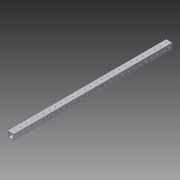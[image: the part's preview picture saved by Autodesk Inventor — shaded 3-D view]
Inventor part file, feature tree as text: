
AUTODESK INVENTOR PART (.ipt)
format: ipt  version: 2014 SP1 (Build 180222100, 222)  size: 189,440 bytes
history: native  units: in
note: dims shown in document units (in); Inventor stores cm internally (conversion verified against a paired STEP export)
features: extrude x3, sketch x3, pattern_linear x2
ambient origin geometry x8: Origin, YZ Plane, XZ Plane, XY Plane, X Axis, Y Axis, Z Axis, Center Point
bodies: Solid1 (feature_tree)
feature tree (8):
  extrude  "Extrusion1"  Depth=1.0in
  extrude  "Extrusion2"  Depth=27.125in TaperAngle=0.0deg
  sketch  "Sketch2"  dims[d2=0.125in d3=27.125in d4=0.0in]
  pattern_linear  "Rectangular Pattern1"  Spacing1=0.164in  [1 undecoded]
  extrude  "Extrusion3"  Depth=1.0in TaperAngle=0.0deg
  pattern_linear  "Rectangular Pattern2"  Count1=27 Spacing1=1.0in
  sketch  "Sketch1"  dims[d0=1.0in d1=1.0in]
  sketch  "Sketch3"  dims[d5=0.5in d6=0.164in d7=1.0in d8=0.0in d9=10.6299in d11=1.0in d12=0.5in d13=0.164in d14=1.0in d15=0.0in d16=10.6299in d18=1.0in]
note: 1 required parameter value undecoded (feature->parameter linkage not recoverable at this tier; creation-order binding heuristic only, values carry confidence <= 0.55)
